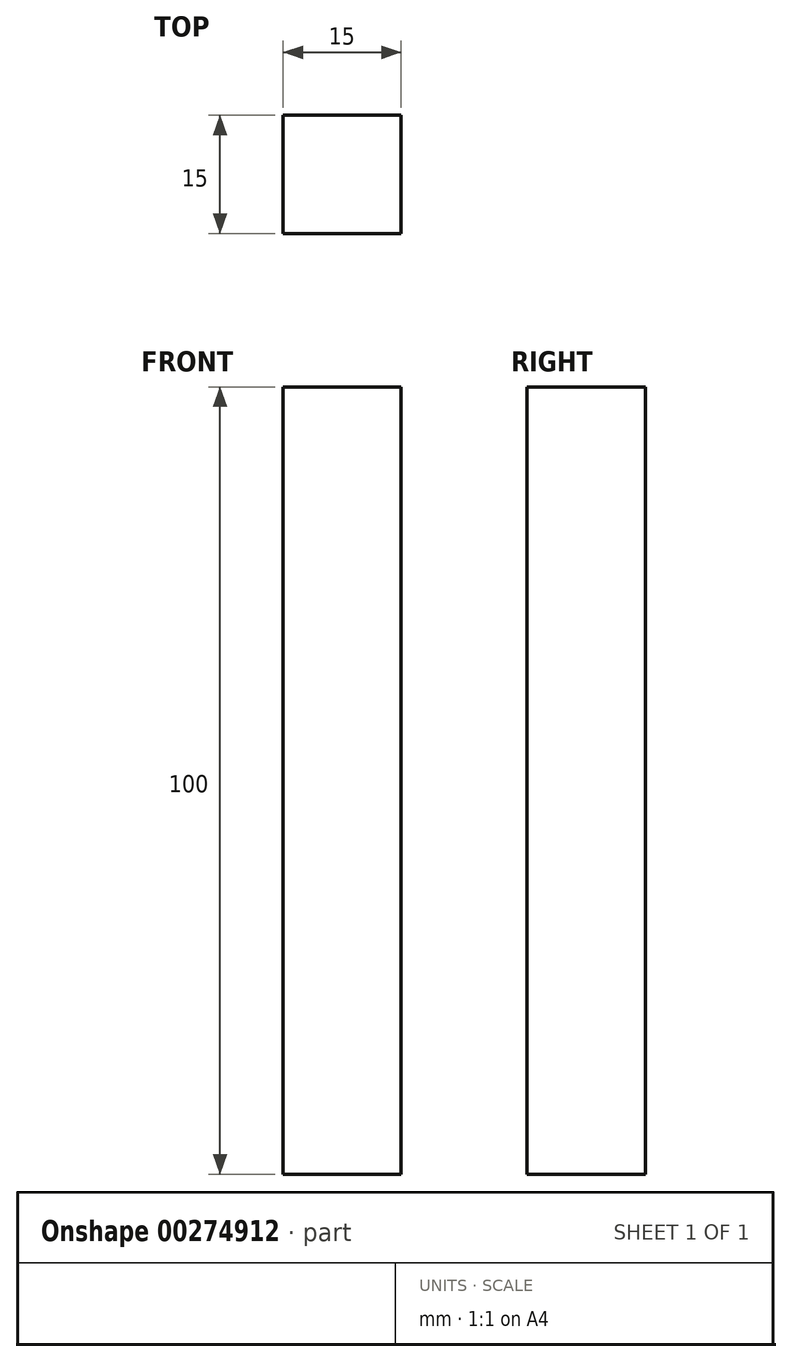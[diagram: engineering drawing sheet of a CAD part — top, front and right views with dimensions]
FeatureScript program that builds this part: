
annotation { "Feature Type Name" : "Feature", "Feature Type Description" : "" }
export const myFeature = defineFeature(function(context is Context, id is Id, definition is map)
    precondition{}
    {
        {
            var Q0;
            Q0=qCreatedBy(makeId("Top.planeOp"),FACE);
            var sketch = newSketch(context, id + "F0", { "sketchPlane" : qUnion([Q0])});
            skLineSegment(sketch, "E0.bottom", {"start": v(-10, -0.07) * mm, "end": v(5, -0.07) * mm});
            skLineSegment(sketch, "E0.top", {"start": v(-10, -15.07) * mm, "end": v(5, -15.07) * mm});
            skLineSegment(sketch, "E0.left", {"start": v(-10, -0.07) * mm, "end": v(-10, -15.07) * mm});
            skLineSegment(sketch, "E0.right", {"start": v(5, -0.07) * mm, "end": v(5, -15.07) * mm});
            skSolve(sketch);
        }
        {
            var Q0;
            Q0 = qSketchRegion(id + "F0", true);
            extrude(context, id + "F1", {"entities" : qUnion([Q0]), "depth" : 100 * mm});
        }
    });
